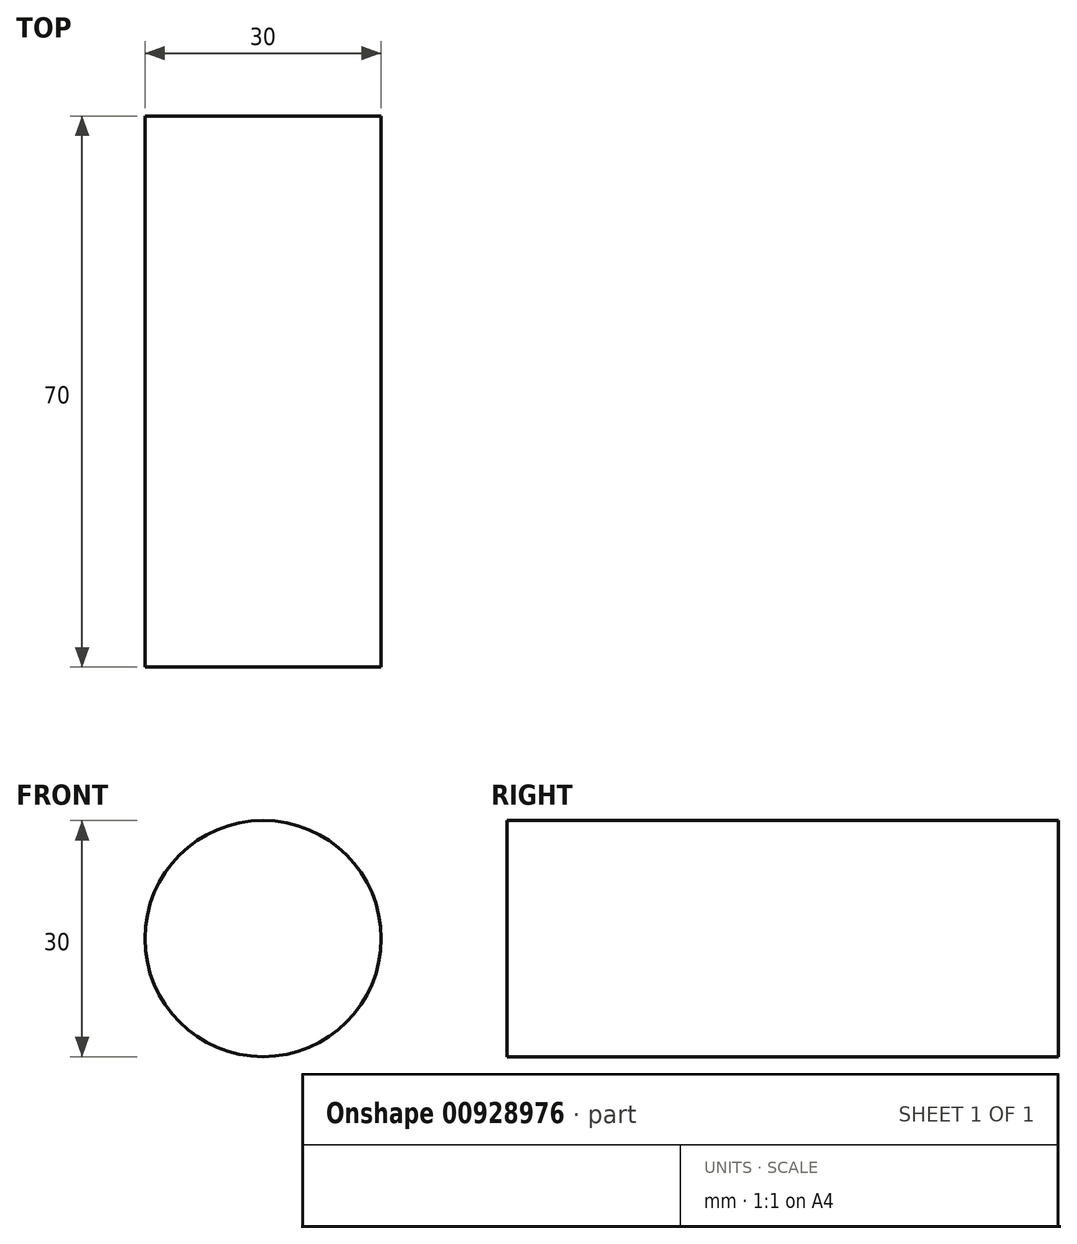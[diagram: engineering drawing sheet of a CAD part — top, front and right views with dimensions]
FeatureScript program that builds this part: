
annotation { "Feature Type Name" : "Feature", "Feature Type Description" : "" }
export const myFeature = defineFeature(function(context is Context, id is Id, definition is map)
    precondition{}
    {
        {
            var Q0;
            Q0=qCreatedBy(makeId("Front.planeOp"),FACE);
            var sketch = newSketch(context, id + "F0", { "sketchPlane" : qUnion([Q0])});
            skCircle(sketch, "E0", {"center": v(0, 0) * mm, "radius": 15 * mm});
            skSolve(sketch);
        }
        {
            var Q0;
            Q0=makeQuery(id+"F0.imprint","IMPRINT",FACE,{"disambiguationData":[TD([[makeQuery(id+"F0.imprint","IMPRINT",EDGE,{"derivedFrom":sQuery(id+"F0.wireOp",EDGE,"E0")}),1.0]])]});
            extrude(context, id + "F1", {"entities" : qUnion([Q0]), "endBound" : BoundingType.SYMMETRIC, "depth" : 70 * mm, "offsetDistance" : 25 * mm});
        }
    });
